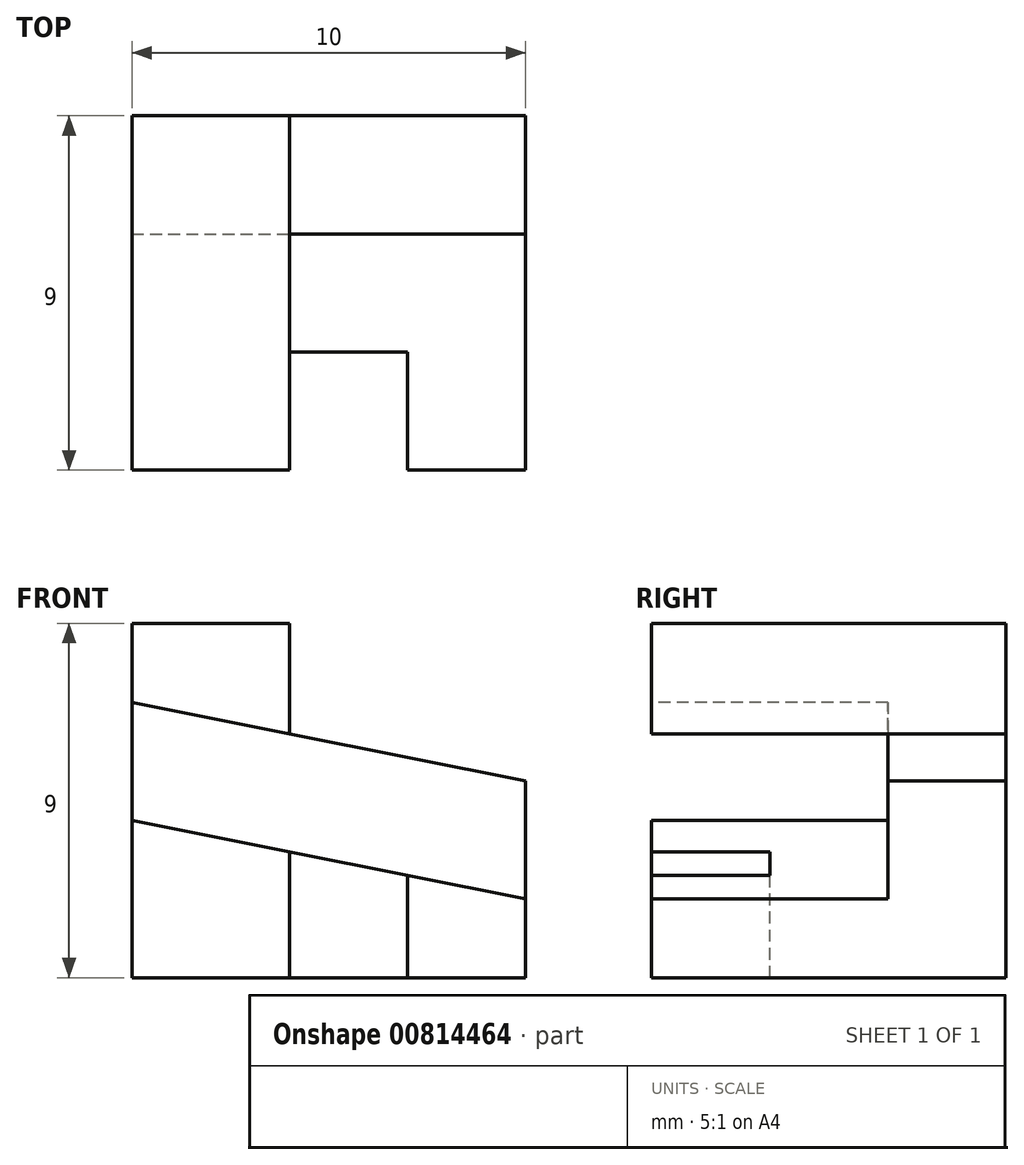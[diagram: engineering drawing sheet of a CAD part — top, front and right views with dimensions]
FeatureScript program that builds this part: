
annotation { "Feature Type Name" : "Feature", "Feature Type Description" : "" }
export const myFeature = defineFeature(function(context is Context, id is Id, definition is map)
    precondition{}
    {
        {
            var Q0;
            Q0=qCreatedBy(makeId("Front.planeOp"),FACE);
            var sketch = newSketch(context, id + "F0", { "sketchPlane" : qUnion([Q0])});
            skLineSegment(sketch, "E0.bottom", {"start": v(0, 0) * mm, "end": v(10, 0) * mm});
            skLineSegment(sketch, "E0.top", {"start": v(0, 9) * mm, "end": v(10, 9) * mm});
            skLineSegment(sketch, "E0.left", {"start": v(0, 0) * mm, "end": v(0, 9) * mm});
            skLineSegment(sketch, "E0.right", {"start": v(10, 0) * mm, "end": v(10, 9) * mm});
            skLineSegment(sketch, "E1", {"start": v(0, 4) * mm, "end": v(10, 2) * mm});
            skLineSegment(sketch, "E2", {"start": v(7, 0) * mm, "end": v(7, 2.6) * mm});
            skLineSegment(sketch, "E3", {"start": v(4, 0) * mm, "end": v(4, 3.2) * mm});
            skLineSegment(sketch, "E4", {"start": v(0, 7) * mm, "end": v(10, 5) * mm});
            skLineSegment(sketch, "E5", {"start": v(4, 6.2) * mm, "end": v(4, 9) * mm});
            skSolve(sketch);
        }
        {
            var Q0;
            {var subQ3=sQuery(id+"F0.wireOp",EDGE,"E3");Q0=makeQuery(id+"F0.imprint","IMPRINT",FACE,{"disambiguationData":[TD([[makeQuery(id+"F0.imprint","IMPRINT",EDGE,{"derivedFrom":subQ3}),1.0]])]});}
            var Q1;
            {var subQ3=sQuery(id+"F0.wireOp",EDGE,"E2");Q1=makeQuery(id+"F0.imprint","IMPRINT",FACE,{"disambiguationData":[TD([[makeQuery(id+"F0.imprint","IMPRINT",EDGE,{"derivedFrom":subQ3}),-1.0]])]});}
            var Q2;
            {var subQ3=sQuery(id+"F0.wireOp",EDGE,"E5");Q2=makeQuery(id+"F0.imprint","IMPRINT",FACE,{"disambiguationData":[TD([[makeQuery(id+"F0.imprint","IMPRINT",EDGE,{"derivedFrom":subQ3}),1.0]])]});}
            var Q3;
            {var subQ0=sQuery(id+"F0.wireOp",EDGE,"E2");Q3=makeQuery(id+"F0.imprint","IMPRINT",FACE,{"disambiguationData":[TD([[makeQuery(id+"F0.imprint","IMPRINT",EDGE,{"derivedFrom":subQ0}),1.0]])]});}
            var Q4;
            {var subQ0=sQuery(id+"F0.wireOp",EDGE,"E1");var subQ7=sQuery(id+"F0.wireOp",EDGE,"E0.left");var subQ8=makeQuery(id+"F0.imprint","INTERSECT",VERTEX,{"derivedFrom":[subQ7,subQ0]});Q4=makeQuery(id+"F0.imprint","IMPRINT",FACE,{"disambiguationData":[TD([[makeQuery(id+"F0.imprint","IMPRINT",EDGE,{"disambiguationData":[TD([[subQ8,-1.0]])],"derivedFrom":subQ7}),-1.0]])]});}
            extrude(context, id + "F1", {"entities" : qUnion([Q0, Q1, Q2, Q3, Q4]), "oppositeDirection" : true, "depth" : 9 * mm, "offsetDistance" : 25 * mm});
        }
        {
            var Q0;
            {var subQ0=sQuery(id+"F0.wireOp",EDGE,"E1");var subQ7=sQuery(id+"F0.wireOp",EDGE,"E0.left");var subQ8=makeQuery(id+"F0.imprint","INTERSECT",VERTEX,{"derivedFrom":[subQ7,subQ0]});Q0=makeQuery(id+"F0.imprint","IMPRINT",FACE,{"disambiguationData":[TD([[makeQuery(id+"F0.imprint","IMPRINT",EDGE,{"disambiguationData":[TD([[subQ8,-1.0]])],"derivedFrom":subQ7}),-1.0]])]});}
            extrude(context, id + "F2", {"entities" : qUnion([Q0]), "operationType" : NewBodyOperationType.REMOVE, "oppositeDirection" : true, "depth" : 6 * mm, "offsetDistance" : 25 * mm});
        }
        {
            var Q0;
            {var subQ0=sQuery(id+"F0.wireOp",EDGE,"E2");Q0=makeQuery(id+"F0.imprint","IMPRINT",FACE,{"disambiguationData":[TD([[makeQuery(id+"F0.imprint","IMPRINT",EDGE,{"derivedFrom":subQ0}),1.0]])]});}
            extrude(context, id + "F3", {"entities" : qUnion([Q0]), "operationType" : NewBodyOperationType.REMOVE, "oppositeDirection" : true, "depth" : 3 * mm, "offsetDistance" : 25 * mm});
        }
    });
